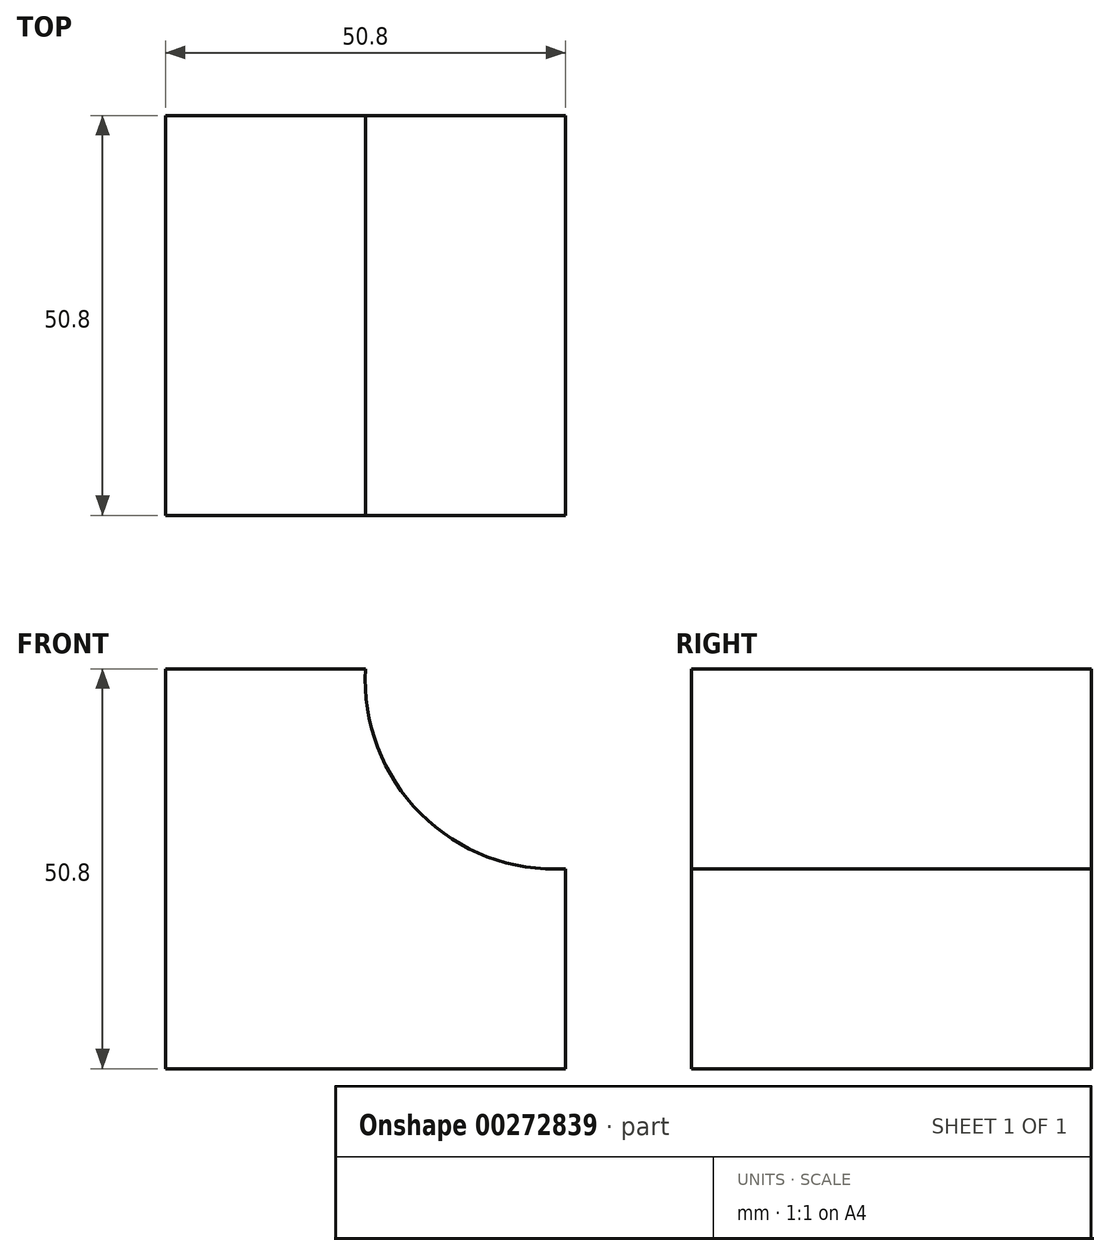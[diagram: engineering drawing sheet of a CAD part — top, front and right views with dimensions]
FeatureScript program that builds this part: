
annotation { "Feature Type Name" : "Feature", "Feature Type Description" : "" }
export const myFeature = defineFeature(function(context is Context, id is Id, definition is map)
    precondition{}
    {
        {
            var Q0;
            Q0=qCreatedBy(makeId("Front.planeOp"),FACE);
            var sketch = newSketch(context, id + "F0", { "sketchPlane" : qUnion([Q0])});
            skLineSegment(sketch, "E0", {"start": v(0, 0) * mm, "end": v(-50.8, 0) * mm});
            skLineSegment(sketch, "E1", {"start": v(-50.8, 0) * mm, "end": v(-50.8, 50.8) * mm});
            skLineSegment(sketch, "E2", {"start": v(-50.8, 50.8) * mm, "end": v(-25.4, 50.8) * mm});
            skLineSegment(sketch, "E3", {"start": v(0, 0) * mm, "end": v(0, 25.4) * mm});
            skArc(sketch, "E4", {"start": v(-25.4, 50.8) * mm, "mid": v(-18.4, 32.4) * mm, "end": v(0, 25.4) * mm});
            skSolve(sketch);
        }
        {
            var Q0;
            Q0=makeQuery(id+"F0.imprint","IMPRINT",FACE,{"disambiguationData":[TD([[makeQuery(id+"F0.imprint","IMPRINT",EDGE,{"derivedFrom":sQuery(id+"F0.wireOp",EDGE,"E0")}),-1.0]])]});
            extrude(context, id + "F1", {"entities" : qUnion([Q0]), "depth" : 50.8 * mm});
        }
    });
